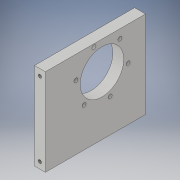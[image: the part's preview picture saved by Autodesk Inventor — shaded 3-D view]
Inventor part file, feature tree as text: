
AUTODESK INVENTOR PART (.ipt)
format: ipt  version: 2019 (Build 230136000, 136)  size: 146,432 bytes
history: native  units: in
note: dims shown in document units (in); Inventor stores cm internally (conversion verified against a paired STEP export)
features: sketch x4, hole x3, projected_geometry x2, extrude x1
ambient origin geometry x8: Origin, YZ Plane, XZ Plane, XY Plane, X Axis, Y Axis, Z Axis, Center Point
bodies: Solid1 (feature_tree)
feature tree (10):
  extrude  "Extrusion1"  Depth=2.3in
  hole  "Hole1"  [1 undecoded]
  hole  "Hole2"  [1 undecoded]
  hole  "Hole4"  [1 undecoded]
  sketch  "Sketch1"  dims[d0=1.0in d1=2.3in]
  sketch  "Sketch2"  dims[d4=1.0in d5=0.65in]
  projected_geometry  "Projected Loop1"
  sketch  "Sketch3"  dims[d6=2.0in d7=0.25in d8=0.0in]
  sketch  "Sketch5"  dims[d9=0.25in d10=0.125in d11=0.125in d12=0.15in d13=0.15in d14=0.076in d15=0.198in d16=0.119in d17=0.25in d18=0.5635in d19=0.302in d20=0.8108in d21=0.613in d22=2.3622in d24=360.0deg d26=0.092in d27=0.198in d28=0.119in d29=0.25in d30=0.5635in d31=0.302in d32=0.8108in d42=0.25in d43=0.25in d44=0.076in d45=0.198in d46=0.375in d47=0.25in d48=0.5635in d49=0.302in d50=0.8108in]
  projected_geometry  "Projected Loop3"
note: 3 required parameter values undecoded (feature->parameter linkage not recoverable at this tier; creation-order binding heuristic only, values carry confidence <= 0.55)
